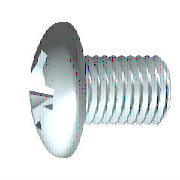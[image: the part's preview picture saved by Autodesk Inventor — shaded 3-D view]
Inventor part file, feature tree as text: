
AUTODESK INVENTOR PART (.ipt)
format: ipt  version: 2013 (Build 170138000, 138)  size: 328,192 bytes
history: native  units: mm (DEFAULTED — no unit token found)
features: extrude x2, other x1, plane x1
ambient origin geometry x7: Origin, YZ Plane, XZ Plane, X Axis, Y Axis, Z Axis, Center Point
bodies: Solid1 (feature_tree), Body (feature_tree)
feature tree (4):
  extrude  "Slot"  Depth=6.35mm
  other  "Cut"
  extrude  "Star Cut"  Depth=4.0386mm
  plane  "Work Plane3"
